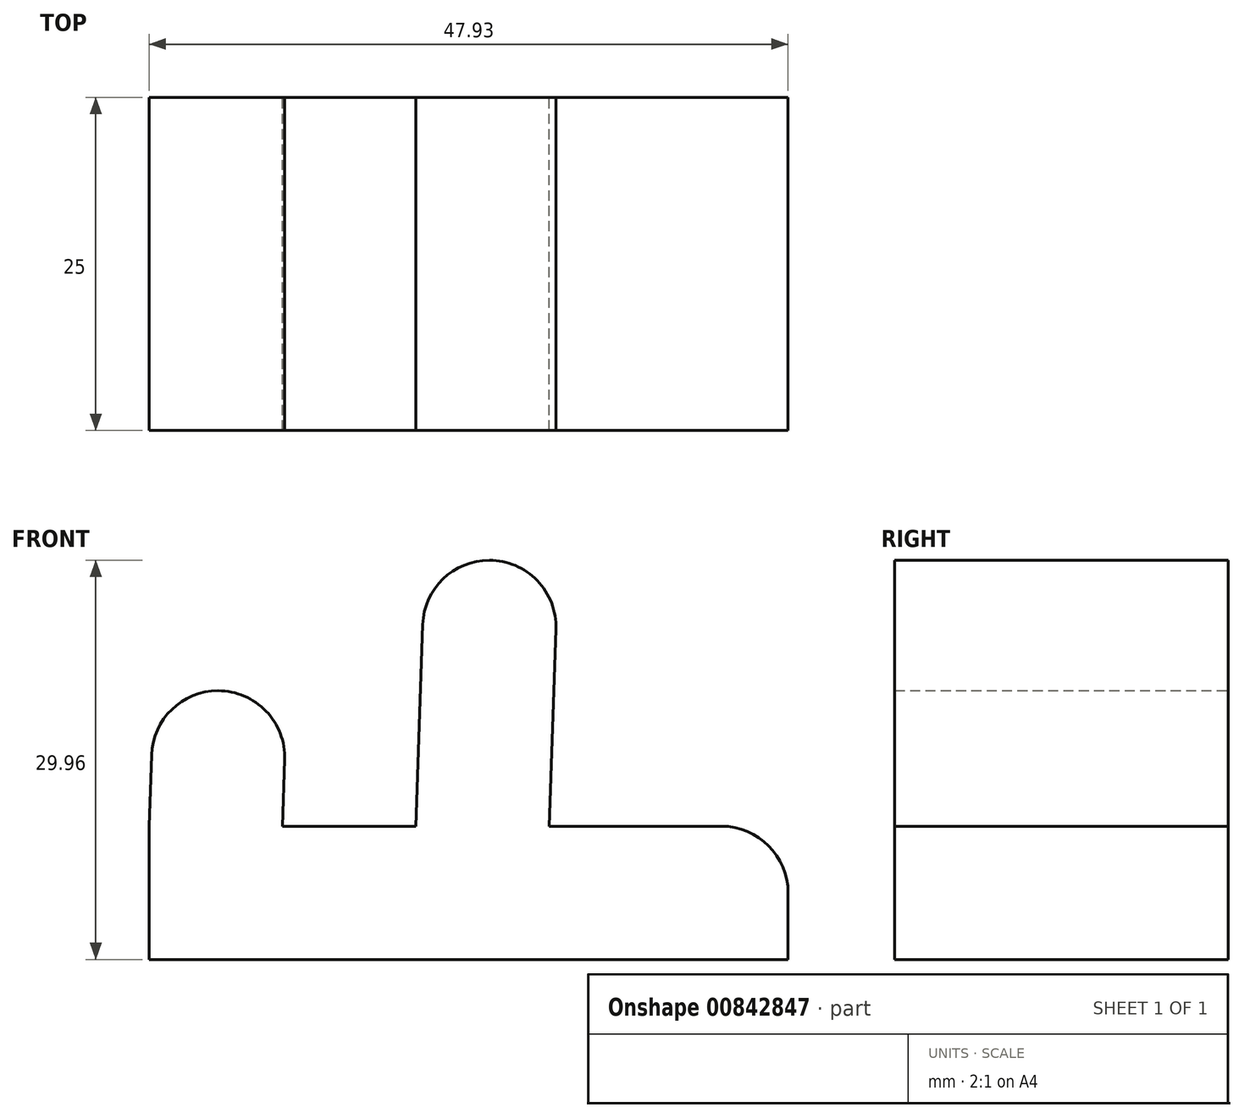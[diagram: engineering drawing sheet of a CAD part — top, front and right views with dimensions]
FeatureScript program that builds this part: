
annotation { "Feature Type Name" : "Feature", "Feature Type Description" : "" }
export const myFeature = defineFeature(function(context is Context, id is Id, definition is map)
    precondition{}
    {
        {
            var Q0;
            Q0=qCreatedBy(makeId("Front.planeOp"),FACE);
            var sketch = newSketch(context, id + "F0", { "sketchPlane" : qUnion([Q0])});
            skPoint(sketch, "E0.middle", {"position": v(0, 0) * mm});
            skLineSegment(sketch, "E1", {"start": v(-30, 3.86) * mm, "end": v(-29.65, 14.02) * mm});
            skLineSegment(sketch, "E2", {"start": v(-29.65, 14.02) * mm, "end": v(-19.65, 14.02) * mm});
            skLineSegment(sketch, "E3", {"start": v(-19.65, 14.02) * mm, "end": v(-20, 3.86) * mm});
            skLineSegment(sketch, "E4", {"start": v(-20, 3.86) * mm, "end": v(-10, 3.86) * mm});
            skLineSegment(sketch, "E5", {"start": v(-10, 3.86) * mm, "end": v(-9.3, 23.82) * mm});
            skLineSegment(sketch, "E6", {"start": v(-9.3, 23.82) * mm, "end": v(0.7, 23.82) * mm});
            skLineSegment(sketch, "E7", {"start": v(0.7, 23.82) * mm, "end": v(0, 3.86) * mm});
            skLineSegment(sketch, "E8.bottom", {"start": v(-30, 3.86) * mm, "end": v(17.93, 3.86) * mm});
            skLineSegment(sketch, "E8.top", {"start": v(-30, -6.14) * mm, "end": v(17.93, -6.14) * mm});
            skLineSegment(sketch, "E8.left", {"start": v(-30, 3.86) * mm, "end": v(-30, -6.14) * mm});
            skLineSegment(sketch, "E8.right", {"start": v(17.93, 3.86) * mm, "end": v(17.93, -6.14) * mm});
            skSolve(sketch);
        }
        {
            var Q0;
            Q0=qSketchRegion(id+"F0",true);
            extrude(context, id + "F1", {"entities" : qUnion([Q0]), "depth" : 25 * mm, "offsetDistance" : 25 * mm});
        }
        {
            var Q0;
            Q0=makeQuery(id+"F1.opExtrude","SWEPT_EDGE",EDGE,{"disambiguationData":[OSD([sQuery(id+"F0.wireOp",EDGE,"E1"),sQuery(id+"F0.wireOp",EDGE,"E2")])]});
            fillet(context, id + "F2", {"entities" : qUnion([Q0]), "radius" : 5 * mm, "tangentPropagation" : true, "allowEdgeOverflow" : false});
        }
        {
            var Q0;
            Q0=makeQuery(id+"F1.opExtrude","SWEPT_EDGE",EDGE,{"disambiguationData":[OSD([sQuery(id+"F0.wireOp",EDGE,"E2"),sQuery(id+"F0.wireOp",EDGE,"E3")])]});
            var Q1;
            Q1=makeQuery(id+"F1.opExtrude","SWEPT_EDGE",EDGE,{"disambiguationData":[OSD([sQuery(id+"F0.wireOp",EDGE,"E5"),sQuery(id+"F0.wireOp",EDGE,"E6")])]});
            fillet(context, id + "F3", {"entities" : qUnion([Q0, Q1]), "radius" : 5 * mm, "tangentPropagation" : true, "allowEdgeOverflow" : false});
        }
        {
            var Q0;
            Q0=makeQuery(id+"F1.opExtrude","SWEPT_EDGE",EDGE,{"disambiguationData":[OSD([sQuery(id+"F0.wireOp",EDGE,"E6"),sQuery(id+"F0.wireOp",EDGE,"E7")])]});
            fillet(context, id + "F4", {"entities" : qUnion([Q0]), "radius" : 5 * mm, "tangentPropagation" : true, "allowEdgeOverflow" : false});
        }
        {
            var Q0;
            Q0=makeQuery(id+"F1.opExtrude","SWEPT_EDGE",EDGE,{"disambiguationData":[OSD([sQuery(id+"F0.wireOp",EDGE,"E8.bottom"),sQuery(id+"F0.wireOp",EDGE,"E8.right")])]});
            fillet(context, id + "F5", {"entities" : qUnion([Q0]), "radius" : 5 * mm, "tangentPropagation" : true, "allowEdgeOverflow" : false});
        }
    });
